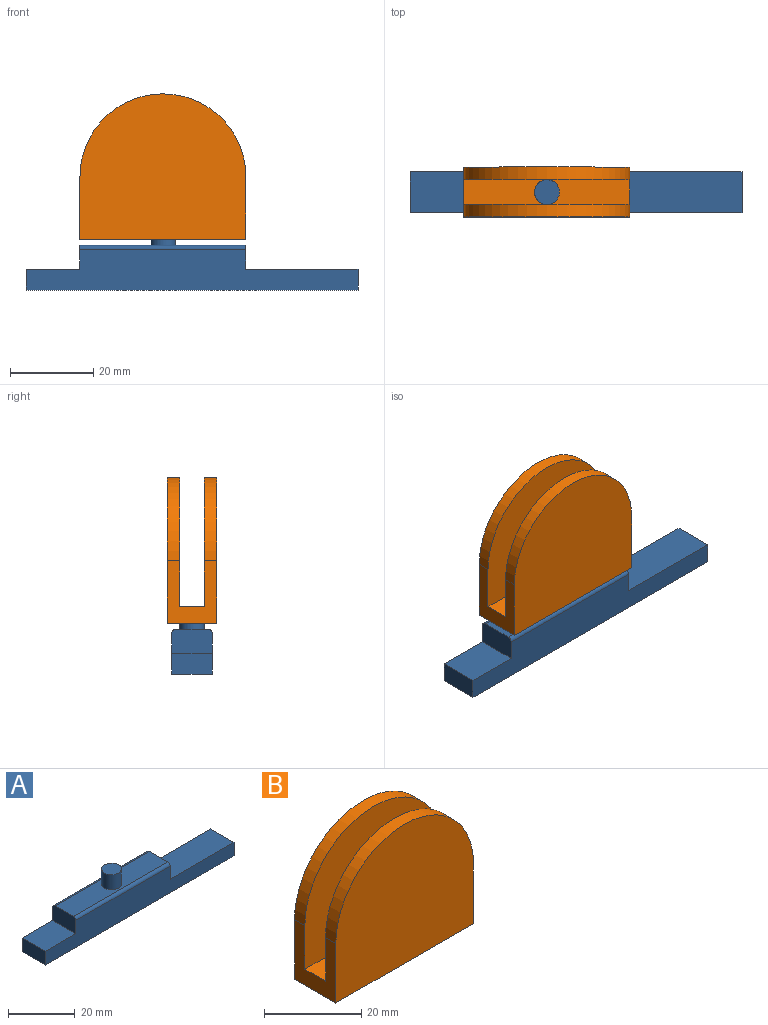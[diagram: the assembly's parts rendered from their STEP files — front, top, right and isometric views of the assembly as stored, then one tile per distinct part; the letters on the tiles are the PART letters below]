
ASSEMBLY  parts=2 mates=1
PART A: 14 faces, bbox 80x9.8x16.3 mm
  f0: plane 9.8x5mm, normal (-1,0,0), area 49mm2, adj f1,f7,f8,f9
  f1: plane 80x9.8mm, normal (0,0,-1), area 784mm2, adj f0,f2,f8,f9
  f2: plane 9.8x5mm, normal (1,0,0), area 49mm2, adj f1,f3,f8,f9
  f3: plane 27x9.8mm, normal (0,0,1), area 264.6mm2, adj f2,f4,f8,f9
  f4: plane 9.8x5.8mm, normal (1,0,0), area 56.4mm2, adj f3,f5,f8,f9,f12,f13
  f5: plane 40x7.8mm, normal (0,0,1), area 283.7mm2, adj f4,f6,f10,f12,f13
  f6: plane 9.8x5.8mm, normal (-1,0,0), area 56.4mm2, adj f5,f7,f8,f9,f12,f13
  f7: plane 13x9.8mm, normal (0,0,1), area 127.4mm2, adj f0,f6,f8,f9
  f8: plane 80x9.8mm, normal (0,-1,0), area 592mm2, adj f0,f1,f2,f3,f4,f6,f7,f13
  f9: plane 80x9.8mm, normal (0,1,0), area 592mm2, adj f0,f1,f2,f3,f4,f6,f7,f12
  f10: cylinder r=3mm len=6mm, axis (0,0,-1), area 103.7mm2, adj f5,f11
  f11: plane 6x6mm, normal (0,0,1), area 28.3mm2, adj f10
  f12: cylinder r=1mm len=40mm, axis (-1,0,0), area 62.8mm2, adj f4,f5,f6,f9
  f13: cylinder r=1mm len=40mm, axis (1,0,0), area 62.8mm2, adj f4,f5,f6,f8
PART B: 12 faces, bbox 40x12x35 mm
  f0: plane 20x6mm, normal (0,0,1), area 105.9mm2, adj f1,f8,f10,f11
  f1: plane 15x12mm, normal (1,0,0), area 114mm2, adj f0,f2,f3,f4,f6,f7,f8,f10
  f2: cylinder r=20mm len=40mm, axis (0,1,0), area 188.5mm2, adj f1,f5,f7,f10
  f3: plane 40x12mm, normal (0,0,-1), area 451.7mm2, adj f1,f5,f6,f7,f11
  f4: cylinder r=20mm len=40mm, axis (0,1,0), area 188.5mm2, adj f1,f5,f6,f8
  f5: plane 15x12mm, normal (-1,0,0), area 114mm2, adj f2,f3,f4,f6,f7,f8,f9,f10
  f6: plane 40x35mm, normal (0,-1,0), area 1228.3mm2, adj f1,f3,f4,f5
  f7: plane 40x35mm, normal (0,1,0), area 1228.3mm2, adj f1,f2,f3,f5
  f8: plane 40x31mm, normal (0,1,0), area 1068.3mm2, adj f0,f1,f4,f5,f9
  f9: plane 20x6mm, normal (0,0,1), area 105.9mm2, adj f5,f8,f10,f11
  f10: plane 40x31mm, normal (0,-1,0), area 1068.3mm2, adj f0,f1,f2,f5,f9
  f11: cylinder r=3mm len=6mm, axis (0,0,-1), area 75.4mm2, adj f0,f3,f9
PLACE A t=(-5.54,1.6,6.7)mm
PLACE B t=(-5.54,1.6,19)mm
MATE revolute A.f10 <-> B.f11  axis (0,0,-1) through (-5.54,1.6,23)mm
